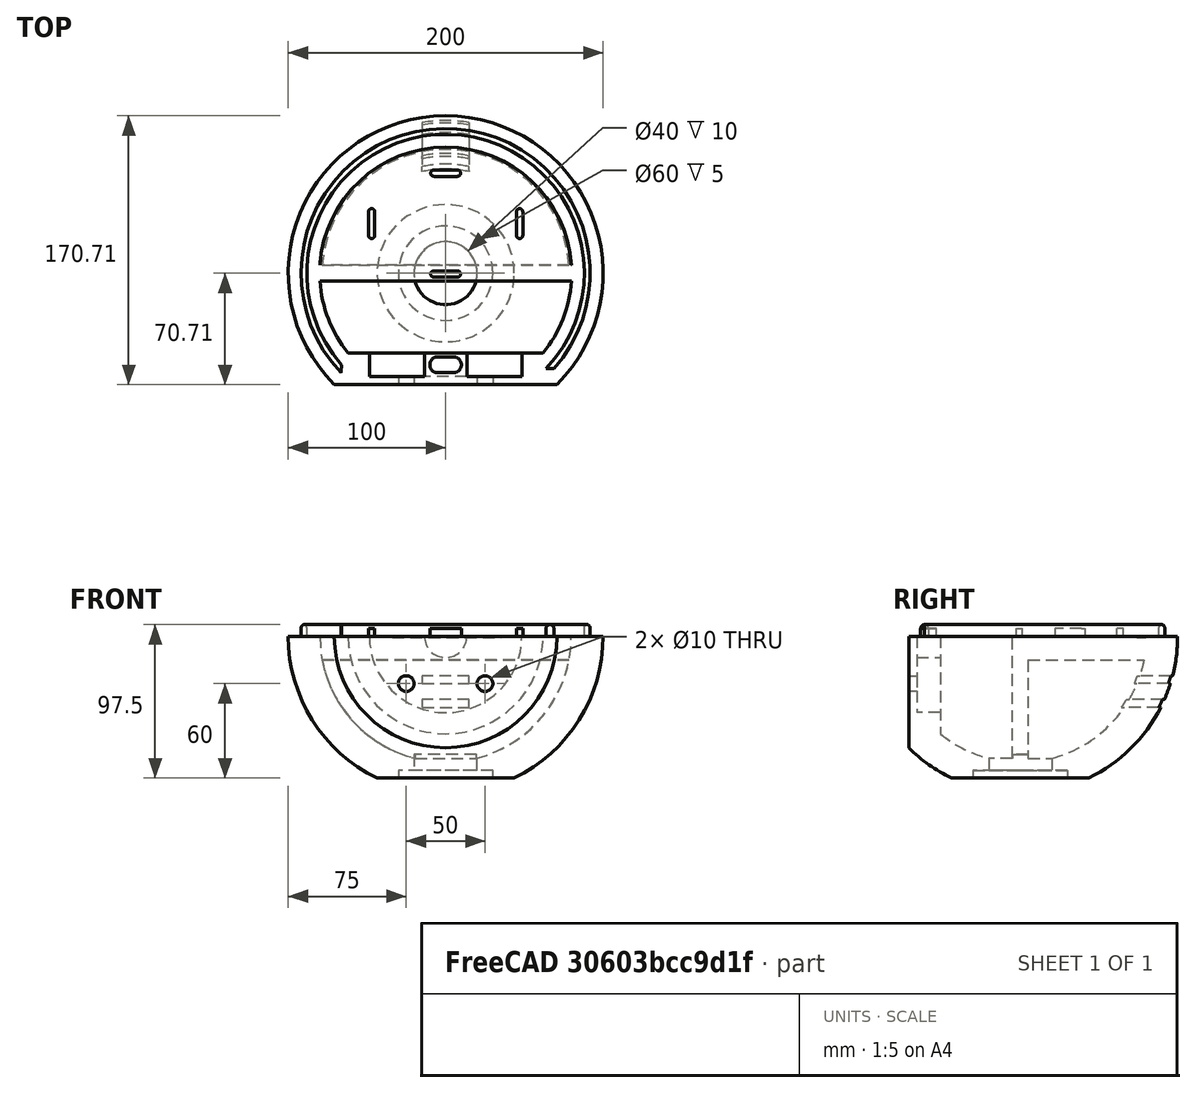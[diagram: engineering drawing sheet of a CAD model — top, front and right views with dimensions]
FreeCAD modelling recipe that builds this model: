
FCSTD DOCUMENT  (FreeCAD 0.18R4 (GitTag))
Label: Ariel Bottom
License: All rights reserved
LicenseURL: http://en.wikipedia.org/wiki/All_rights_reserved
objects: Sketcher::SketchObject×12, Part::Plane×7, PartDesign::Pocket×6, PartDesign::Pad×3, PartDesign::Revolution×1, PartDesign::AdditivePipe×1, PartDesign::Mirrored×1, PartDesign::Body×1, Mesh::Feature×1
note: 43 computed .brp shape members not serialized (recipe doc carries the construction recipe); baked Part::Feature solids carry a one-line shape summary decoded from their .brp

FEATURE [Sketcher::SketchObject] Sketch
  sketch-geometry (21):
    g0: ArcOfCircle CenterX=0 CenterY=0 CenterZ=0 NormalX=0 NormalY=0 NormalZ=1 AngleXU=0 Radius=100 StartAngle=5.49779 EndAngle=7.85398
    g1: LineSegment StartX=3.06e-14 StartY=100 StartZ=0 EndX=-2e-16 EndY=80 EndZ=0
    g2: LineSegment [constr] StartX=0 StartY=0 StartZ=0 EndX=106.066 EndY=-106.066 EndZ=0
    g3: LineSegment StartX=70.7107 StartY=-70.7107 StartZ=0 EndX=0 EndY=-70.7107 EndZ=0
    g4: LineSegment StartX=61.8736 StartY=-50.7107 StartZ=0 EndX=48.4368 EndY=-50.7107 EndZ=0
    g5: LineSegment StartX=48.4368 StartY=-50.7107 StartZ=0 EndX=48.4368 EndY=-65.7107 EndZ=0
    g6: LineSegment StartX=48.4368 StartY=-65.7107 StartZ=0 EndX=13.4368 EndY=-65.7107 EndZ=0
    g7: LineSegment StartX=13.4368 StartY=-65.7107 StartZ=0 EndX=13.4368 EndY=-50.7107 EndZ=0
    g8: LineSegment StartX=13.4368 StartY=-50.7107 StartZ=0 EndX=0 EndY=-50.7107 EndZ=0
    g9: LineSegment StartX=0 StartY=-50.7107 StartZ=0 EndX=0 EndY=-70.7107 EndZ=0
    g10: LineSegment [constr] StartX=0 StartY=0 StartZ=0 EndX=106.066 EndY=106.066 EndZ=0
    g11: GeomPoint X=56.5685 Y=56.5685 Z=0
    g12: GeomPoint X=70.7107 Y=70.7107 Z=0
    g13: GeomPoint X=100 Y=0 Z=0
    g14: GeomPoint X=80 Y=0 Z=0
    g15: LineSegment StartX=0 StartY=5 StartZ=0 EndX=79.84 EndY=5 EndZ=0
    g16: LineSegment StartX=0 StartY=-5 StartZ=0 EndX=79.84 EndY=-5 EndZ=0
    g17: LineSegment StartX=0 StartY=5 StartZ=0 EndX=0 EndY=-5 EndZ=0
    g18: ArcOfCircle CenterX=-0.00383734 CenterY=-0.0038376 CenterZ=0 NormalX=0 NormalY=0 NormalZ=1 AngleXU=0 Radius=80 StartAngle=5.59668 EndAngle=6.22069
    g19: GeomPoint X=56.5685 Y=-56.5685 Z=0
    g20: ArcOfCircle CenterX=-0.00359712 CenterY=8.08704e-08 CenterZ=0 NormalX=0 NormalY=0 NormalZ=1 AngleXU=0 Radius=80 StartAngle=0.0625408 EndAngle=1.57075
  constraints (58):
    c: Coincident(g0,g-1)
    c: PointOnObject(g0,g-2)
    c: Radius(g0) = 100
    c: PointOnObject(g1,g-2)
    c: DistanceY(g1,g0) = 20
    c: Coincident(g1,g0)
    c: Coincident(g2,g0)
    c: Angle(g2,g-1) = 0.785398
    c: Distance(g2) = 150
    c: PointOnObject(g0,g2)
    c: Coincident(g3,g0)
    c: PointOnObject(g3,g-2)
    c: Horizontal(g3)
    c: Horizontal(g4)
    c: Coincident(g5,g4)
    c: Vertical(g5)
    c: Coincident(g6,g5)
    c: Horizontal(g6)
    c: Coincident(g7,g6)
    c: Vertical(g7)
    c: Coincident(g8,g7)
    c: PointOnObject(g8,g-2)
    c: Coincident(g9,g8)
    c: Coincident(g9,g3)
    c: DistanceX(g6,g6) = 35
    c: Horizontal(g8,g4)
    c: Horizontal(g8)
    c: DistanceY(g3,g6) = 5
    c: Equal(g1,g9)
    c: Coincident(g10,g0)
    c: Symmetric(g10,g2,g-1)
    c: PointOnObject(g12,g0)
    c: PointOnObject(g11,g10)
    c: PointOnObject(g12,g10)
    c: Distance(g12,g11) = 20
    c: PointOnObject(g13,g0)
    c: PointOnObject(g14,g-1)
    c: PointOnObject(g13,g-1)
    c: Distance(g14,g13) = 20
    c: Equal(g4,g8)
    c: PointOnObject(g15,g-2)
    c: Horizontal(g15)
    c: Horizontal(g16)
    c: Coincident(g17,g15)
    c: Coincident(g17,g16)
    c: Symmetric(g15,g16,g-1)
    c: DistanceY(g17,g17) = 10
    c: Coincident(g18,g16)
    c: Coincident(g18,g4)
    c: PointOnObject(g19,g2)
    c: Distance(g19,g0) = 20
    c: PointOnObject(g19,g18)
    c: Coincident(g20,g1)
    c: Coincident(g20,g15)
    c: DistanceX(g16,g16) = 79.84
    c: Equal(g16,g15)
    c: Radius(g20) = 80
    c: Radius(g18) = 80
FEATURE [PartDesign::Revolution] Revolution
  Angle = 180
  Axis = (0,1,0)
  Base = (0,0,0)
  Profile = -> Sketch
  ReferenceAxis = -> Sketch [V_Axis]
FEATURE [Sketcher::SketchObject] Sketch001
  ExternalGeometry = -> [Revolution]
  MapMode = 5
  Support = -> [XY_Plane]
  sketch-geometry (6):
    g0: LineSegment [constr] StartX=61.8736 StartY=-50.7107 StartZ=0 EndX=70.7107 EndY=-70.7107 EndZ=0
    g1: LineSegment [constr] StartX=-61.8736 StartY=-50.7107 StartZ=0 EndX=-70.7107 EndY=-70.7107 EndZ=0
    g2: GeomPoint X=-66.2921 Y=-60.7107 Z=0
    g3: GeomPoint X=66.2921 Y=-60.7107 Z=0
    g4: ArcOfCircle CenterX=5.2e-15 CenterY=0.0649239 CenterZ=0 NormalX=0 NormalY=0 NormalZ=1 AngleXU=0 Radius=89.9351 StartAngle=5.54117 EndAngle=10.1668
    g5: GeomPoint X=0 Y=90 Z=0
  constraints (13):
    c: Coincident(g0,g-13)
    c: Coincident(g0,g-19)
    c: Coincident(g1,g-16)
    c: Coincident(g1,g-20)
    c: PointOnObject(g2,g1)
    c: Distance(g2,g1) = 10.9327
    c: PointOnObject(g3,g0)
    c: Horizontal(g3,g2)
    c: Coincident(g4,g2)
    c: Coincident(g4,g3)
    c: PointOnObject(g5,g4)
    c: PointOnObject(g5,g-2)
    c: DistanceY(g5,g-18) = 10
FEATURE [Part::Plane] Plane
  AttacherType = Attacher::AttachEngine3D
  Length = 10
  Placement = pos=(0,-60.711,0) rot=(0.57735,0.57735,0.57735;4.18879rad)
  Width = 10
FEATURE [Sketcher::SketchObject] Sketch002
  ExternalGeometry = -> [Revolution]
  MapMode = 5
  Placement = pos=(0,-60.711,0) rot=(0.57735,0.57735,0.57735;4.18879rad)
  Support = -> [Plane]
  sketch-geometry (4):
    g0: ArcOfCircle CenterX=5 CenterY=66.2921 CenterZ=0 NormalX=0 NormalY=0 NormalZ=1 AngleXU=0 Radius=2.5 StartAngle=4.71239 EndAngle=7.85398
    g1: ArcOfCircle CenterX=-5 CenterY=66.2921 CenterZ=0 NormalX=0 NormalY=0 NormalZ=1 AngleXU=0 Radius=2.5 StartAngle=1.5708 EndAngle=4.71239
    g2: LineSegment StartX=5 StartY=68.7921 StartZ=0 EndX=-5 EndY=68.7921 EndZ=0
    g3: LineSegment StartX=5 StartY=63.7921 StartZ=0 EndX=-5 EndY=63.7921 EndZ=0
  constraints (9):
    c: Tangent(g0,g3) = 1.5708
    c: Tangent(g0,g2) = -1.5708
    c: Tangent(g2,g1) = -1.5708
    c: Tangent(g3,g1) = 1.5708
    c: Horizontal(g2)
    c: DistanceX(g2,g2) = 10
    c: Radius(g0) = 2.5
    c: Symmetric(g0,g1,g-2)
    c: DistanceY(g-3,g0) = 4.41853
FEATURE [PartDesign::AdditivePipe] AdditivePipe
  AuxilleryCurvelinear = true
  AuxillerySpineTangent = false
  BaseFeature = -> Revolution
  Binormal = (0,0,0)
  Mode = 0
  Profile = -> Sketch002
  Spine = -> Sketch001
  SpineTangent = false
  Transformation = 0
  Transition = 0
FEATURE [Part::Plane] Plane001
  AttacherType = Attacher::AttachEngine3D
  Length = 10
  Placement = pos=(100,0,0) rot=(0.57735,0.57735,0.57735;2.0944rad)
  Width = 10
FEATURE [Sketcher::SketchObject] Sketch003
  MapMode = 5
  Placement = pos=(100,0,0) rot=(0.57735,0.57735,0.57735;2.0944rad)
  Support = -> [Plane001]
  sketch-geometry (4):
    g0: LineSegment StartX=-50 StartY=-100 StartZ=0 EndX=50 EndY=-100 EndZ=0
    g1: LineSegment StartX=50 StartY=-100 StartZ=0 EndX=50 EndY=-90 EndZ=0
    g2: LineSegment StartX=50 StartY=-90 StartZ=0 EndX=-50 EndY=-90 EndZ=0
    g3: LineSegment StartX=-50 StartY=-90 StartZ=0 EndX=-50 EndY=-100 EndZ=0
  constraints (11):
    c: Coincident(g0,g1)
    c: Coincident(g1,g2)
    c: Coincident(g2,g3)
    c: Coincident(g3,g0)
    c: Horizontal(g2)
    c: Vertical(g1)
    c: Vertical(g3)
    c: Symmetric(g0,g0,g-2)
    c: DistanceY(g3,g3) = 10
    c: DistanceX(g2,g2) = 100
    c: DistanceY(g0,g-1) = 100
FEATURE [PartDesign::Pocket] Pocket
  BaseFeature = -> AdditivePipe
  Length = 5
  Length2 = 100
  Profile = -> Sketch003
  Type = 1
FEATURE [Part::Plane] Plane002
  AttacherType = Attacher::AttachEngine3D
  Length = 10
  Placement = pos=(0,100,0) rot=(0.57735,0.57735,0.57735;4.18879rad)
  Width = 10
FEATURE [Part::Plane] Plane003
  AttacherType = Attacher::AttachEngine3D
  Length = 10
  Placement = pos=(0,95,0) rot=(0.57735,0.57735,0.57735;4.18879rad)
  Width = 10
FEATURE [Sketcher::SketchObject] Sketch005
  MapMode = 5
  Placement = pos=(0,95,0) rot=(0.57735,0.57735,0.57735;4.18879rad)
  Support = -> [Plane003]
  sketch-geometry (4):
    g0: LineSegment StartX=-40 StartY=15 StartZ=0 EndX=-45 EndY=15 EndZ=0
    g1: LineSegment StartX=-45 StartY=15 StartZ=0 EndX=-45 EndY=-15 EndZ=0
    g2: LineSegment StartX=-45 StartY=-15 StartZ=0 EndX=-40 EndY=-15 EndZ=0
    g3: LineSegment StartX=-40 StartY=-15 StartZ=0 EndX=-40 EndY=15 EndZ=0
  constraints (11):
    c: Coincident(g0,g1)
    c: Coincident(g1,g2)
    c: Coincident(g2,g3)
    c: Coincident(g3,g0)
    c: Horizontal(g2)
    c: Vertical(g1)
    c: DistanceY(g1,g1) = 30
    c: DistanceX(g0,g0) = 5
    c: Symmetric(g0,g2,g-1)
    c: Horizontal(g0)
    c: DistanceX(g2,g-1) = 40
FEATURE [Part::Plane] Plane004
  AttacherType = Attacher::AttachEngine3D
  Length = 10
  Placement = pos=(0,100,0) rot=(0.57735,0.57735,0.57735;4.18879rad)
  Width = 10
FEATURE [Sketcher::SketchObject] Sketch006
  MapMode = 5
  Placement = pos=(0,100,0) rot=(0.57735,0.57735,0.57735;4.18879rad)
  Support = -> [Plane004]
  sketch-geometry (4):
    g0: LineSegment StartX=-25 StartY=15 StartZ=0 EndX=-30 EndY=15 EndZ=0
    g1: LineSegment StartX=-30 StartY=15 StartZ=0 EndX=-30 EndY=-15 EndZ=0
    g2: LineSegment StartX=-30 StartY=-15 StartZ=0 EndX=-25 EndY=-15 EndZ=0
    g3: LineSegment StartX=-25 StartY=-15 StartZ=0 EndX=-25 EndY=15 EndZ=0
  constraints (11):
    c: Coincident(g0,g1)
    c: Coincident(g1,g2)
    c: Coincident(g2,g3)
    c: Coincident(g3,g0)
    c: Horizontal(g2)
    c: Vertical(g1)
    c: DistanceY(g1,g1) = 30
    c: DistanceX(g0,g0) = 5
    c: Symmetric(g0,g2,g-1)
    c: Horizontal(g0)
    c: DistanceX(g2,g-1) = 25
FEATURE [PartDesign::Pocket] Pocket002
  BaseFeature = -> Pocket
  Length = 50
  Length2 = 100
  Profile = -> Sketch005
  Type = 0
FEATURE [PartDesign::Pocket] Pocket003
  BaseFeature = -> Pocket002
  Length = 40
  Length2 = 100
  Profile = -> Sketch006
  Type = 0
FEATURE [Sketcher::SketchObject] Sketch007
  ExternalGeometry = -> [Pocket003]
  MapMode = 5
  Support = -> [XY_Plane]
  sketch-geometry (4):
    g0: ArcOfCircle CenterX=-5 CenterY=-58.2107 CenterZ=0 NormalX=0 NormalY=0 NormalZ=1 AngleXU=0 Radius=5 StartAngle=1.5708 EndAngle=4.71239
    g1: ArcOfCircle CenterX=5 CenterY=-58.2107 CenterZ=0 NormalX=0 NormalY=0 NormalZ=1 AngleXU=0 Radius=5 StartAngle=4.71239 EndAngle=7.85398
    g2: LineSegment StartX=-5 StartY=-63.2107 StartZ=0 EndX=5 EndY=-63.2107 EndZ=0
    g3: LineSegment StartX=-5 StartY=-53.2107 StartZ=0 EndX=5 EndY=-53.2107 EndZ=0
  constraints (9):
    c: Tangent(g0,g3) = 1.5708
    c: Tangent(g0,g2) = -1.5708
    c: Tangent(g2,g1) = -1.5708
    c: Tangent(g3,g1) = 1.5708
    c: Horizontal(g2)
    c: DistanceX(g2,g2) = 10
    c: Radius(g1) = 5
    c: Symmetric(g0,g1,g-2)
    c: DistanceY(g-6,g0) = 7.5
FEATURE [PartDesign::Pad] Pad
  BaseFeature = -> Pocket003
  Length = 5
  Length2 = 100
  Profile = -> Sketch007
  Type = 0
FEATURE [Sketcher::SketchObject] Sketch008
  ExternalGeometry = -> [Pad]
  MapMode = 5
  Support = -> [XY_Plane]
  sketch-geometry (2):
    g0: LineSegment StartX=-79.84 StartY=5 StartZ=0 EndX=79.84 EndY=5 EndZ=0
    g1: ArcOfCircle CenterX=2.8e-15 CenterY=0.000225335 CenterZ=0 NormalX=0 NormalY=0 NormalZ=1 AngleXU=0 Radius=79.9964 StartAngle=0.0625408 EndAngle=3.07905
  constraints (5):
    c: Coincident(g1,g0)
    c: Coincident(g1,g0)
    c: Tangent(g1,g-6)
    c: Coincident(g0,g-6)
    c: Coincident(g0,g-5)
FEATURE [PartDesign::Pad] Pad001
  BaseFeature = -> Pad
  Length = 15
  Length2 = 100
  Profile = -> Sketch008
  Reversed = true
  Type = 0
FEATURE [Part::Plane] Plane005
  AttacherType = Attacher::AttachEngine3D
  Length = 10
  Placement = pos=(0,0,-90) rot=(0,0,1;0rad)
  Width = 10
FEATURE [Sketcher::SketchObject] Sketch009
  MapMode = 5
  Placement = pos=(0,0,-90) rot=(0,0,1;0rad)
  Support = -> [Plane005]
  sketch-geometry (1):
    g0: Circle CenterX=0 CenterY=0 CenterZ=0 NormalX=0 NormalY=0 NormalZ=1 AngleXU=0 Radius=30
  constraints (2):
    c: Coincident(g0,g-1)
    c: Radius(g0) = 30
FEATURE [PartDesign::Pocket] Pocket004
  BaseFeature = -> Pad001
  Length = 5
  Length2 = 100
  Profile = -> Sketch009
  Reversed = true
  Type = 0
FEATURE [Sketcher::SketchObject] Sketch010
  MapMode = 5
  Placement = pos=(0,0,-90) rot=(0,0,1;0rad)
  Support = -> [Plane005]
  sketch-geometry (1):
    g0: Circle CenterX=0 CenterY=0 CenterZ=0 NormalX=0 NormalY=0 NormalZ=1 AngleXU=0 Radius=20
  constraints (2):
    c: Coincident(g0,g-1)
    c: Radius(g0) = 20
FEATURE [PartDesign::Pocket] Pocket005
  BaseFeature = -> Pocket004
  Length = 15
  Length2 = 100
  Profile = -> Sketch010
  Reversed = true
  Type = 0
FEATURE [Sketcher::SketchObject] Sketch011
  MapMode = 5
  Support = -> [XY_Plane]
  sketch-geometry (16):
    g0: ArcOfCircle CenterX=-7.5 CenterY=63.5 CenterZ=0 NormalX=0 NormalY=0 NormalZ=1 AngleXU=0 Radius=2 StartAngle=1.5708 EndAngle=4.71239
    g1: ArcOfCircle CenterX=7.5 CenterY=63.5 CenterZ=0 NormalX=0 NormalY=0 NormalZ=1 AngleXU=0 Radius=2 StartAngle=4.71239 EndAngle=7.85398
    g2: LineSegment StartX=-7.5 StartY=61.5 StartZ=0 EndX=7.5 EndY=61.5 EndZ=0
    g3: LineSegment StartX=-7.5 StartY=65.5 StartZ=0 EndX=7.5 EndY=65.5 EndZ=0
    g4: ArcOfCircle CenterX=-47 CenterY=39 CenterZ=0 NormalX=0 NormalY=0 NormalZ=1 AngleXU=0 Radius=2 StartAngle=-1.8e-15 EndAngle=3.14159
    g5: ArcOfCircle CenterX=-47 CenterY=24 CenterZ=0 NormalX=0 NormalY=0 NormalZ=1 AngleXU=0 Radius=2 StartAngle=3.14159 EndAngle=6.28319
    g6: LineSegment StartX=-49 StartY=39 StartZ=0 EndX=-49 EndY=24 EndZ=0
    g7: LineSegment StartX=-45 StartY=39 StartZ=0 EndX=-45 EndY=24 EndZ=0
    g8: ArcOfCircle CenterX=-7.5 CenterY=-0.5 CenterZ=0 NormalX=0 NormalY=0 NormalZ=1 AngleXU=0 Radius=2 StartAngle=1.5708 EndAngle=4.71239
    g9: ArcOfCircle CenterX=7.5 CenterY=-0.5 CenterZ=0 NormalX=0 NormalY=0 NormalZ=1 AngleXU=0 Radius=2 StartAngle=4.71239 EndAngle=7.85398
    g10: LineSegment StartX=-7.5 StartY=-2.5 StartZ=0 EndX=7.5 EndY=-2.5 EndZ=0
    g11: LineSegment StartX=-7.5 StartY=1.5 StartZ=0 EndX=7.5 EndY=1.5 EndZ=0
    g12: ArcOfCircle CenterX=47 CenterY=39 CenterZ=0 NormalX=0 NormalY=0 NormalZ=1 AngleXU=0 Radius=2 StartAngle=-9e-16 EndAngle=3.14159
    g13: ArcOfCircle CenterX=47 CenterY=24 CenterZ=0 NormalX=0 NormalY=0 NormalZ=1 AngleXU=0 Radius=2 StartAngle=3.14159 EndAngle=6.28319
    g14: LineSegment StartX=45 StartY=39 StartZ=0 EndX=45 EndY=24 EndZ=0
    g15: LineSegment StartX=49 StartY=39 StartZ=0 EndX=49 EndY=24 EndZ=0
  constraints (37):
    c: Tangent(g0,g3) = 1.5708
    c: Tangent(g0,g2) = -1.5708
    c: Tangent(g2,g1) = -1.5708
    c: Tangent(g3,g1) = 1.5708
    c: Horizontal(g2)
    c: Tangent(g4,g7) = 1.5708
    c: Tangent(g4,g6) = -1.5708
    c: Tangent(g6,g5) = -1.5708
    c: Tangent(g7,g5) = 1.5708
    c: Vertical(g6)
    c: Equal(g4,g5)
    c: Tangent(g8,g11) = 1.5708
    c: Tangent(g8,g10) = -1.5708
    c: Tangent(g10,g9) = -1.5708
    c: Tangent(g11,g9) = 1.5708
    c: Horizontal(g10)
    c: Tangent(g12,g15) = 1.5708
    c: Tangent(g12,g14) = -1.5708
    c: Tangent(g14,g13) = -1.5708
    c: Tangent(g15,g13) = 1.5708
    c: Vertical(g14)
    c: Equal(g12,g13)
    c: Symmetric(g1,g0,g-2)
    c: Radius(g1) = 2
    c: Symmetric(g9,g8,g-2)
    c: Equal(g9,g0)
    c: Equal(g12,g8)
    c: Equal(g13,g5)
    c: Symmetric(g12,g4,g-2)
    c: DistanceX(g4,g12) = 90
    c: Equal(g14,g6)
    c: DistanceY(g6,g6) = 15
    c: Equal(g6,g2)
    c: Equal(g2,g11)
    c: DistanceY(g8,g0) = 60
    c: DistanceY(g-1,g9) = -2.5
    c: DistanceY(g4,g0) = 22.5
FEATURE [PartDesign::Pad] Pad002
  BaseFeature = -> Pocket005
  Length = 5
  Length2 = 100
  Profile = -> Sketch011
  Type = 0
FEATURE [Part::Plane] Plane006
  AttacherType = Attacher::AttachEngine3D
  Length = 10
  Placement = pos=(0,-75,0) rot=(0.57735,0.57735,0.57735;4.18879rad)
  Width = 10
FEATURE [Sketcher::SketchObject] Sketch012
  MapMode = 5
  Placement = pos=(0,-75,0) rot=(0.57735,0.57735,0.57735;4.18879rad)
  Support = -> [Plane006]
  sketch-geometry (1):
    g0: Circle CenterX=-30 CenterY=25 CenterZ=0 NormalX=0 NormalY=0 NormalZ=1 AngleXU=0 Radius=5
  constraints (3):
    c: Radius(g0) = 5
    c: DistanceY(g-1,g0) = 25
    c: DistanceX(g0,g-1) = 30
FEATURE [PartDesign::Pocket] Pocket006
  BaseFeature = -> Pad002
  Length = 10
  Length2 = 100
  Profile = -> Sketch012
  Reversed = true
  Type = 0
FEATURE [PartDesign::Mirrored] Mirrored
  BaseFeature = -> Pocket006
  MirrorPlane = -> YZ_Plane
  Originals = -> [Pocket006]
FEATURE [PartDesign::Body] Body
  Group = -> [Sketch,Revolution,Sketch001,Sketch002,AdditivePipe,Sketch003,Pocket,Sketch005,Sketch006,Pocket002,Pocket003,Sketch007,Pad,Sketch008,Pad001,Sketch009,Pocket004,Sketch010,Pocket005,Sketch011,Pad002,Sketch012,Pocket006,Mirrored]
  Origin = -> Origin
  Tip = -> Mirrored
FEATURE [Mesh::Feature] Mesh  label="Body (Meshed)"
